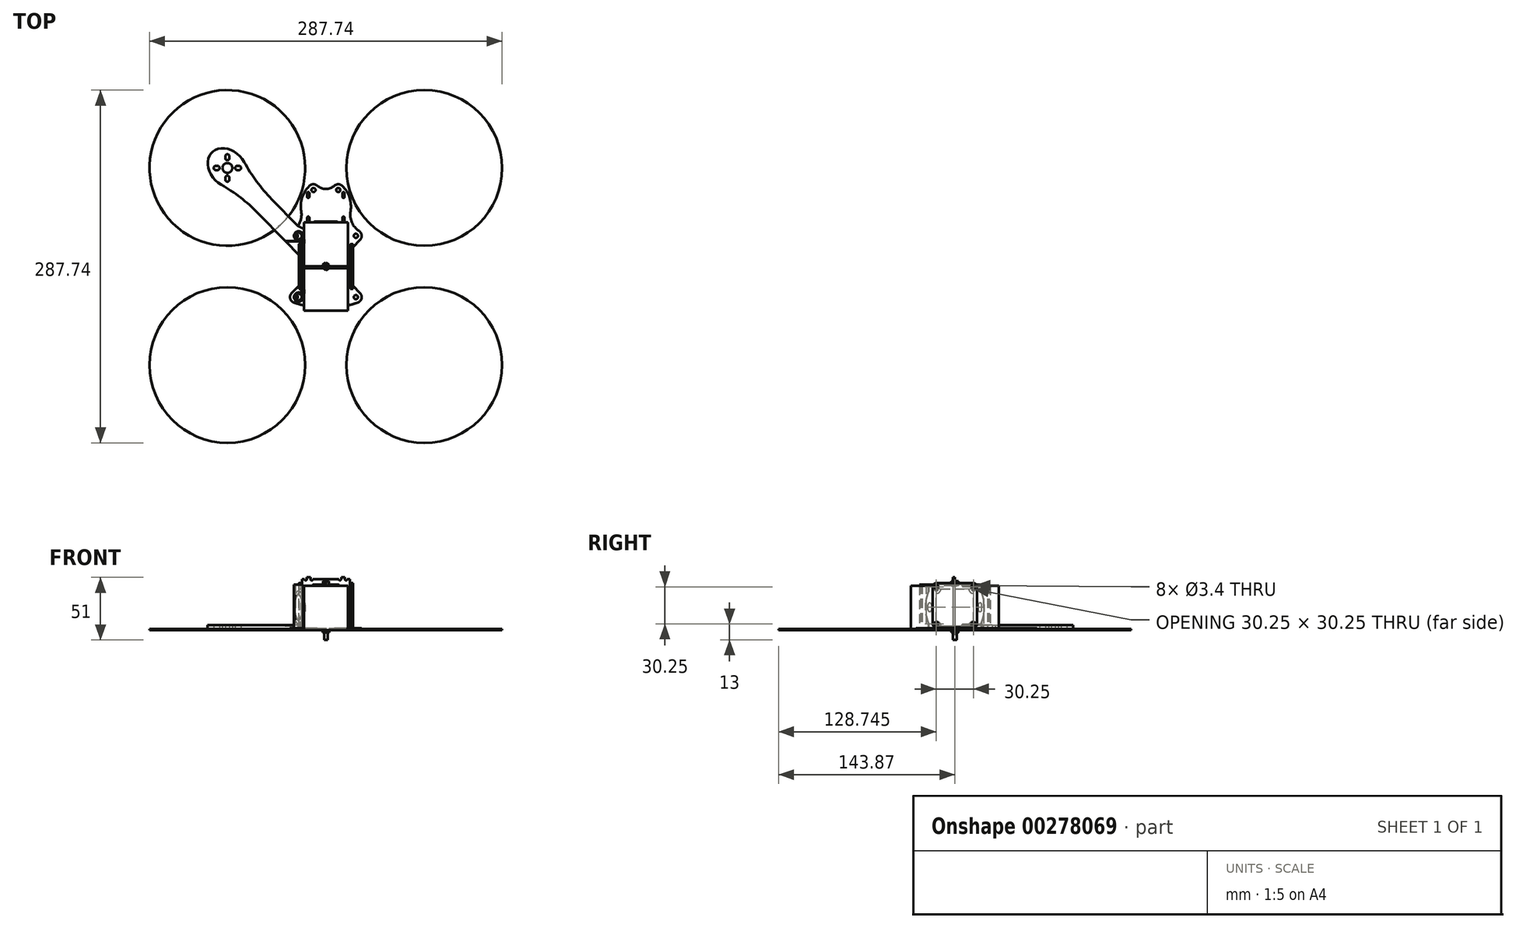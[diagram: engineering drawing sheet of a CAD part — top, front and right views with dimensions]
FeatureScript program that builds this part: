
annotation { "Feature Type Name" : "Feature", "Feature Type Description" : "" }
export const myFeature = defineFeature(function(context is Context, id is Id, definition is map)
    precondition{}
    {
        {
            var Q0;
            Q0=qCreatedBy(makeId("Top.planeOp"),FACE);
            var sketch = newSketch(context, id + "F0", { "sketchPlane" : qUnion([Q0])});
            skLineSegment(sketch, "E0.bottom", {"start": v(-18, 36) * mm, "end": v(18, 36) * mm});
            skLineSegment(sketch, "E0.top", {"start": v(-18, -36) * mm, "end": v(18, -36) * mm});
            skLineSegment(sketch, "E0.left", {"start": v(-18, 36) * mm, "end": v(-18, -36) * mm});
            skLineSegment(sketch, "E0.right", {"start": v(18, 36) * mm, "end": v(18, -36) * mm});
            skPoint(sketch, "E0.middle", {"position": v(0, 0) * mm});
            skSolve(sketch);
        }
        {
            var Q0;
            Q0 = qSketchRegion(id + "F0", true);
            extrude(context, id + "F1", {"entities" : qUnion([Q0]), "depth" : 36 * mm});
        }
        {
            var Q0;
            Q0=qCreatedBy(makeId("Right.planeOp"),FACE);
            cPlane(context, id + "F2", {"entities" : qUnion([Q0]), "cplaneType" : CPlaneType.OFFSET, "offset" : 20 * mm, "oppositeDirection" : true, "width" : 152.4 * mm, "height" : 152.4 * mm});
        }
        {
            var Q0;
            Q0=qCreatedBy(id+"F2.planeOp",FACE);
            var sketch = newSketch(context, id + "F3", { "sketchPlane" : qUnion([Q0])});
            skLineSegment(sketch, "E1.bottom", {"start": v(15.12, 38.25) * mm, "end": v(-15.12, 38.25) * mm});
            skLineSegment(sketch, "E1.top", {"start": v(15.13, 2) * mm, "end": v(-15.13, 2) * mm});
            skLineSegment(sketch, "E1.left", {"start": v(18.13, 35.25) * mm, "end": v(18.13, 5) * mm});
            skLineSegment(sketch, "E1.right", {"start": v(-18.12, 35.25) * mm, "end": v(-18.13, 5) * mm});
            skPoint(sketch, "E2.visualSharp", {"position": v(18.12, 38.25) * mm});
            skArc(sketch, "E2.filletArc", {"start": v(18.12, 35.25) * mm, "mid": v(17.25, 37.37) * mm, "end": v(15.12, 38.25) * mm});
            skPoint(sketch, "E3.visualSharp", {"position": v(-18.12, 38.25) * mm});
            skArc(sketch, "E3.filletArc", {"start": v(-15.12, 38.25) * mm, "mid": v(-17.25, 37.37) * mm, "end": v(-18.12, 35.25) * mm});
            skPoint(sketch, "E4.visualSharp", {"position": v(-18.13, 2) * mm});
            skArc(sketch, "E4.filletArc", {"start": v(-18.13, 5) * mm, "mid": v(-17.25, 2.88) * mm, "end": v(-15.13, 2) * mm});
            skPoint(sketch, "E5.visualSharp", {"position": v(18.13, 2) * mm});
            skArc(sketch, "E5.filletArc", {"start": v(15.13, 2) * mm, "mid": v(17.25, 2.88) * mm, "end": v(18.13, 5) * mm});
            skCircle(sketch, "E6", {"center": v(15.12, 35.25) * mm, "radius": 1.7 * mm});
            skCircle(sketch, "E7", {"center": v(15.13, 5) * mm, "radius": 1.7 * mm});
            skCircle(sketch, "E8", {"center": v(-15.12, 35.25) * mm, "radius": 1.7 * mm});
            skCircle(sketch, "E9", {"center": v(-15.13, 5) * mm, "radius": 1.7 * mm});
            skSolve(sketch);
        }
        {
            var Q0;
            Q0 = qSketchRegion(id + "F3", true);
            extrude(context, id + "F4", {"entities" : qUnion([Q0]), "oppositeDirection" : true, "depth" : 2 * mm});
        }
        {
            var Q0;
            Q0=makeQuery(id+"F4.opExtrude","SWEPT_BODY",BODY,{"disambiguationData":[OSD([sQuery(id+"F3.wireOp",EDGE,"E1.bottom"),sQuery(id+"F3.wireOp",EDGE,"E1.top"),sQuery(id+"F3.wireOp",EDGE,"E1.left"),sQuery(id+"F3.wireOp",EDGE,"E1.right"),sQuery(id+"F3.wireOp",EDGE,"E2.filletArc"),sQuery(id+"F3.wireOp",EDGE,"E3.filletArc"),sQuery(id+"F3.wireOp",EDGE,"E4.filletArc"),sQuery(id+"F3.wireOp",EDGE,"E5.filletArc"),sQuery(id+"F3.wireOp",EDGE,"E6"),sQuery(id+"F3.wireOp",EDGE,"E7"),sQuery(id+"F3.wireOp",EDGE,"E8"),sQuery(id+"F3.wireOp",EDGE,"E9")])]});
            var Q1;
            Q1=qCreatedBy(makeId("Right.planeOp"),FACE);
            mirror(context, id + "F5", {"entities" : qUnion([Q0]), "mirrorPlane" : qUnion([Q1])});
        }
        {
            var Q0;
            Q0=qCreatedBy(makeId("Top.planeOp"),FACE);
            var sketch = newSketch(context, id + "F6", { "sketchPlane" : qUnion([Q0])});
            skArc(sketch, "E10", {"start": v(-18.5, 25) * mm, "mid": v(-25.6, 26.68) * mm, "end": v(-20, 22) * mm});
            skArc(sketch, "E11", {"start": v(-20, -22) * mm, "mid": v(-25.6, -26.68) * mm, "end": v(-18.5, -25) * mm});
            skLineSegment(sketch, "E12", {"start": v(-18.5, 25) * mm, "end": v(-18.5, -25) * mm});
            skLineSegment(sketch, "E13", {"start": v(-20, 22) * mm, "end": v(-20, -22) * mm});
            skLineSegment(sketch, "E14.0", {"start": v(-22.25, 28.06) * mm, "end": v(-19.6, 26.53) * mm});
            skLineSegment(sketch, "E14.1", {"start": v(-19.6, 26.53) * mm, "end": v(-19.6, 23.47) * mm});
            skLineSegment(sketch, "E14.2", {"start": v(-19.6, 23.47) * mm, "end": v(-22.25, 21.94) * mm});
            skLineSegment(sketch, "E14.3", {"start": v(-22.25, 21.94) * mm, "end": v(-24.9, 23.47) * mm});
            skLineSegment(sketch, "E14.4", {"start": v(-24.9, 23.47) * mm, "end": v(-24.9, 26.53) * mm});
            skLineSegment(sketch, "E14.5", {"start": v(-24.9, 26.53) * mm, "end": v(-22.25, 28.06) * mm});
            skLineSegment(sketch, "E15.0", {"start": v(-22.25, -21.94) * mm, "end": v(-19.6, -23.47) * mm});
            skLineSegment(sketch, "E15.1", {"start": v(-19.6, -23.47) * mm, "end": v(-19.6, -26.53) * mm});
            skLineSegment(sketch, "E15.2", {"start": v(-19.6, -26.53) * mm, "end": v(-22.25, -28.06) * mm});
            skLineSegment(sketch, "E15.3", {"start": v(-22.25, -28.06) * mm, "end": v(-24.9, -26.53) * mm});
            skLineSegment(sketch, "E15.4", {"start": v(-24.9, -26.53) * mm, "end": v(-24.9, -23.47) * mm});
            skLineSegment(sketch, "E15.5", {"start": v(-24.9, -23.47) * mm, "end": v(-22.25, -21.94) * mm});
            skSolve(sketch);
        }
        {
            var Q0;
            Q0 = qSketchRegion(id + "F6", true);
            extrude(context, id + "F7", {"entities" : qUnion([Q0]), "depth" : 37 * mm});
        }
        {
            var Q0;
            Q0=makeQuery(id+"F7.opExtrude","SWEPT_FACE",FACE,{"disambiguationData":[OSD([sQuery(id+"F6.wireOp",EDGE,"E13")])]});
            var sketch = newSketch(context, id + "F8", { "sketchPlane" : qUnion([Q0])});
            skCircle(sketch, "E16", {"center": v(-15.13, 33.62) * mm, "radius": 1.73 * mm});
            skCircle(sketch, "E17", {"center": v(-15.13, 3.38) * mm, "radius": 1.73 * mm});
            skCircle(sketch, "E18", {"center": v(15.13, 33.62) * mm, "radius": 1.73 * mm});
            skCircle(sketch, "E19", {"center": v(15.12, 3.38) * mm, "radius": 1.73 * mm});
            skSolve(sketch);
        }
        {
            var Q0;
            Q0 = qSketchRegion(id + "F8", true);
            extrude(context, id + "F9", {"entities" : qUnion([Q0]), "operationType" : NewBodyOperationType.REMOVE, "oppositeDirection" : true, "depth" : 2 * mm});
        }
        {
            var Q0;
            Q0=makeQuery(id+"F7.opExtrude","SWEPT_BODY",BODY,{"disambiguationData":[OSD([sQuery(id+"F6.wireOp",EDGE,"E10"),sQuery(id+"F6.wireOp",EDGE,"E11"),sQuery(id+"F6.wireOp",EDGE,"E12"),sQuery(id+"F6.wireOp",EDGE,"E13"),sQuery(id+"F6.wireOp",EDGE,"E14.0"),sQuery(id+"F6.wireOp",EDGE,"E14.1"),sQuery(id+"F6.wireOp",EDGE,"E14.2"),sQuery(id+"F6.wireOp",EDGE,"E14.3"),sQuery(id+"F6.wireOp",EDGE,"E14.4"),sQuery(id+"F6.wireOp",EDGE,"E14.5"),sQuery(id+"F6.wireOp",EDGE,"E15.0"),sQuery(id+"F6.wireOp",EDGE,"E15.1"),sQuery(id+"F6.wireOp",EDGE,"E15.2"),sQuery(id+"F6.wireOp",EDGE,"E15.3"),sQuery(id+"F6.wireOp",EDGE,"E15.4"),sQuery(id+"F6.wireOp",EDGE,"E15.5")])]});
            transform(context, id + "F10", {"entities" : qUnion([Q0]), "transformType" : TransformType.TRANSLATION_3D, "dx" : 0 * mm, "dy" : 0 * mm, "dz" : 0 * mm, "makeCopy" : true});
        }
        {
            var Q0;
            Q0=makeQuery(id+"F7.opExtrude","SWEPT_FACE",FACE,{"disambiguationData":[OSD([sQuery(id+"F6.wireOp",EDGE,"E13")])]});
            var sketch = newSketch(context, id + "F11", { "sketchPlane" : qUnion([Q0])});
            skLineSegment(sketch, "E20", {"start": v(-15.13, 29.9) * mm, "end": v(-15.12, 7.1) * mm});
            skLineSegment(sketch, "E21", {"start": v(-11.4, 3.38) * mm, "end": v(11.4, 3.38) * mm});
            skLineSegment(sketch, "E22", {"start": v(15.12, 29.9) * mm, "end": v(15.13, 7.1) * mm});
            skLineSegment(sketch, "E23", {"start": v(-11.4, 33.62) * mm, "end": v(11.4, 33.62) * mm});
            skArc(sketch, "E24", {"start": v(15.13, 7.1) * mm, "mid": v(12.5, 6) * mm, "end": v(11.4, 3.38) * mm});
            skArc(sketch, "E25", {"start": v(11.4, 33.63) * mm, "mid": v(12.5, 31) * mm, "end": v(15.12, 29.9) * mm});
            skArc(sketch, "E26", {"start": v(-11.4, 33.62) * mm, "mid": v(-12.5, 31) * mm, "end": v(-15.13, 29.9) * mm});
            skArc(sketch, "E27", {"start": v(-15.13, 7.1) * mm, "mid": v(-12.5, 6) * mm, "end": v(-11.4, 3.38) * mm});
            skSolve(sketch);
        }
        {
            var Q0;
            Q0 = qSketchRegion(id + "F11", true);
            extrude(context, id + "F12", {"entities" : qUnion([Q0]), "operationType" : NewBodyOperationType.REMOVE, "oppositeDirection" : true, "depth" : 2 * mm});
        }
        {
            var Q0;
            Q0=qCreatedBy(makeId("Top.planeOp"),FACE);
            var sketch = newSketch(context, id + "F13", { "sketchPlane" : qUnion([Q0])});
            skCircle(sketch, "E28.cCircle", {"center": v(0, 0) * mm, "radius": 2.5 * mm, "construction": true});
            skLineSegment(sketch, "E28.0", {"start": v(-2.5, 1.44) * mm, "end": v(0, 2.89) * mm});
            skLineSegment(sketch, "E28.1", {"start": v(0, 2.89) * mm, "end": v(2.5, 1.44) * mm});
            skLineSegment(sketch, "E28.2", {"start": v(2.5, 1.44) * mm, "end": v(2.5, -1.44) * mm});
            skLineSegment(sketch, "E28.3", {"start": v(2.5, -1.44) * mm, "end": v(0, -2.89) * mm});
            skLineSegment(sketch, "E28.4", {"start": v(0, -2.89) * mm, "end": v(-2.5, -1.44) * mm});
            skLineSegment(sketch, "E28.5", {"start": v(-2.5, -1.44) * mm, "end": v(-2.5, 1.44) * mm});
            skPoint(sketch, "E28.0.midPoint", {"position": v(-1.25, 2.17) * mm});
            skCircle(sketch, "E29", {"center": v(0, 0) * mm, "radius": 1.65 * mm});
            skSolve(sketch);
        }
        {
            var Q0;
            Q0 = qSketchRegion(id + "F13", true);
            extrude(context, id + "F14", {"entities" : qUnion([Q0]), "depth" : 40 * mm});
        }
        {
            var Q0;
            Q0=qCreatedBy(makeId("Top.planeOp"),FACE);
            var sketch = newSketch(context, id + "F15", { "sketchPlane" : qUnion([Q0])});
            skCircle(sketch, "E30", {"center": v(0, 0) * mm, "radius": 2.75 * mm});
            skCircle(sketch, "E31.cCircle", {"center": v(0, 0) * mm, "radius": 1.15 * mm, "construction": true});
            skLineSegment(sketch, "E31.0", {"start": v(-0.58, 1) * mm, "end": v(0.58, 1) * mm});
            skLineSegment(sketch, "E31.1", {"start": v(0.58, 1) * mm, "end": v(1.15, 0) * mm});
            skLineSegment(sketch, "E31.2", {"start": v(1.15, 0) * mm, "end": v(0.58, -1) * mm});
            skLineSegment(sketch, "E31.3", {"start": v(0.58, -1) * mm, "end": v(-0.58, -1) * mm});
            skLineSegment(sketch, "E31.4", {"start": v(-0.58, -1) * mm, "end": v(-1.15, 0) * mm});
            skLineSegment(sketch, "E31.5", {"start": v(-1.15, 0) * mm, "end": v(-0.58, 1) * mm});
            skCircle(sketch, "E32", {"center": v(0, 0) * mm, "radius": 1.5 * mm});
            skSolve(sketch);
        }
        {
            var Q0;
            Q0=makeQuery(id+"F15.imprint","IMPRINT",FACE,{"disambiguationData":[TD([[makeQuery(id+"F15.imprint","IMPRINT",EDGE,{"derivedFrom":sQuery(id+"F15.wireOp",EDGE,"E31.0")}),1.0]])]});
            var Q1;
            Q1=makeQuery(id+"F15.imprint","IMPRINT",FACE,{"disambiguationData":[TD([[makeQuery(id+"F15.imprint","IMPRINT",EDGE,{"derivedFrom":sQuery(id+"F15.wireOp",EDGE,"E31.0")}),-1.0]])]});
            extrude(context, id + "F16", {"entities" : qUnion([Q0, Q1]), "oppositeDirection" : true, "depth" : 8 * mm});
        }
        {
            var Q0;
            Q0=makeQuery(id+"F15.imprint","IMPRINT",FACE,{"disambiguationData":[TD([[makeQuery(id+"F15.imprint","IMPRINT",EDGE,{"derivedFrom":sQuery(id+"F15.wireOp",EDGE,"E30")}),1.0]])]});
            var Q1;
            Q1=makeQuery(id+"F15.imprint","IMPRINT",FACE,{"disambiguationData":[TD([[makeQuery(id+"F15.imprint","IMPRINT",EDGE,{"derivedFrom":sQuery(id+"F15.wireOp",EDGE,"E31.0")}),1.0]])]});
            var Q2;
            Q2=makeQuery(id+"F15.imprint","IMPRINT",FACE,{"disambiguationData":[TD([[makeQuery(id+"F15.imprint","IMPRINT",EDGE,{"derivedFrom":sQuery(id+"F15.wireOp",EDGE,"E31.0")}),-1.0]])]});
            extrude(context, id + "F17", {"entities" : qUnion([Q0, Q1, Q2]), "operationType" : NewBodyOperationType.ADD, "oppositeDirection" : true, "depth" : 2 * mm});
        }
        {
            var Q0;
            Q0=makeQuery(id+"F15.imprint","IMPRINT",FACE,{"disambiguationData":[TD([[makeQuery(id+"F15.imprint","IMPRINT",EDGE,{"derivedFrom":sQuery(id+"F15.wireOp",EDGE,"E31.0")}),-1.0]])]});
            extrude(context, id + "F18", {"entities" : qUnion([Q0]), "operationType" : NewBodyOperationType.REMOVE, "oppositeDirection" : true, "depth" : 1.5 * mm});
        }
        {
            var Q0;
            Q0=qCreatedBy(makeId("Top.planeOp"),FACE);
            var sketch = newSketch(context, id + "F19", { "sketchPlane" : qUnion([Q0])});
            skCircle(sketch, "E33.cCircle", {"center": v(0, 0) * mm, "radius": 3.18 * mm, "construction": true});
            skLineSegment(sketch, "E33.0", {"start": v(-1.59, 2.75) * mm, "end": v(1.59, 2.75) * mm});
            skLineSegment(sketch, "E33.1", {"start": v(1.59, 2.75) * mm, "end": v(3.18, 0) * mm});
            skLineSegment(sketch, "E33.2", {"start": v(3.18, 0) * mm, "end": v(1.59, -2.75) * mm});
            skLineSegment(sketch, "E33.3", {"start": v(1.59, -2.75) * mm, "end": v(-1.59, -2.75) * mm});
            skLineSegment(sketch, "E33.4", {"start": v(-1.59, -2.75) * mm, "end": v(-3.18, 0) * mm});
            skLineSegment(sketch, "E33.5", {"start": v(-3.18, 0) * mm, "end": v(-1.59, 2.75) * mm});
            skCircle(sketch, "E34", {"center": v(0, 0) * mm, "radius": 1.5 * mm});
            skSolve(sketch);
        }
        {
            var Q0;
            Q0 = qSketchRegion(id + "F19", true);
            extrude(context, id + "F20", {"entities" : qUnion([Q0]), "depth" : 1.8 * mm});
        }
        {
            var Q0;
            Q0=makeQuery(id+"F10.opPattern","COPY",FACE,{"derivedFrom":makeQuery(id+"F7.opExtrude","SWEPT_FACE",FACE,{"disambiguationData":[OSD([sQuery(id+"F6.wireOp",EDGE,"E13")])]}),"instanceName":"1"});
            var sketch = newSketch(context, id + "F21", { "sketchPlane" : qUnion([Q0])});
            skLineSegment(sketch, "E35", {"start": v(-22, 20.5) * mm, "end": v(-22, 16.5) * mm});
            skLineSegment(sketch, "E36", {"start": v(-19, 16.5) * mm, "end": v(-19, 20.5) * mm});
            skLineSegment(sketch, "E37", {"start": v(22, 20.5) * mm, "end": v(22, 16.5) * mm});
            skLineSegment(sketch, "E38", {"start": v(19, 16.5) * mm, "end": v(19, 20.5) * mm});
            skArc(sketch, "E39", {"start": v(-22, 20.5) * mm, "mid": v(-20.5, 22) * mm, "end": v(-19, 20.5) * mm});
            skArc(sketch, "E40", {"start": v(19, 20.5) * mm, "mid": v(20.5, 22) * mm, "end": v(22, 20.5) * mm});
            skArc(sketch, "E41", {"start": v(-19, 16.5) * mm, "mid": v(-20.5, 15) * mm, "end": v(-22, 16.5) * mm});
            skArc(sketch, "E42", {"start": v(19, 16.5) * mm, "mid": v(20.5, 15) * mm, "end": v(22, 16.5) * mm});
            skSolve(sketch);
        }
        {
            var Q0;
            Q0=qCreatedBy(makeId("Top.planeOp"),FACE);
            var sketch = newSketch(context, id + "F22", { "sketchPlane" : qUnion([Q0])});
            skCircle(sketch, "E43", {"center": v(-24.5, 25) * mm, "radius": 1.7 * mm});
            skCircle(sketch, "E44", {"center": v(24.5, 25) * mm, "radius": 1.7 * mm});
            skCircle(sketch, "E45", {"center": v(24.5, -25) * mm, "radius": 1.7 * mm});
            skCircle(sketch, "E46", {"center": v(-24.5, -25) * mm, "radius": 1.7 * mm});
            skLineSegment(sketch, "E47", {"start": v(-18, 11.62) * mm, "end": v(-18, -11.62) * mm});
            skLineSegment(sketch, "E48", {"start": v(18, 11.62) * mm, "end": v(18, -11.62) * mm});
            skLineSegment(sketch, "E49", {"start": v(18, 11.62) * mm, "end": v(27.87, 21.7) * mm});
            skLineSegment(sketch, "E50", {"start": v(18, -11.62) * mm, "end": v(27.87, -21.7) * mm});
            skLineSegment(sketch, "E51", {"start": v(-18, -11.62) * mm, "end": v(-27.87, -21.7) * mm});
            skLineSegment(sketch, "E52", {"start": v(-18, 11.62) * mm, "end": v(-27.87, 21.7) * mm});
            skArc(sketch, "E53", {"start": v(-27.87, 21.7) * mm, "mid": v(-29.2, 25.5) * mm, "end": v(-27.1, 28.94) * mm});
            skArc(sketch, "E54", {"start": v(27.87, 21.7) * mm, "mid": v(29.2, 25.5) * mm, "end": v(27.1, 28.94) * mm});
            skArc(sketch, "E55", {"start": v(27.87, -21.7) * mm, "mid": v(29.1, -26.09) * mm, "end": v(26.04, -29.47) * mm});
            skArc(sketch, "E56", {"start": v(-27.87, -21.7) * mm, "mid": v(-29.1, -26.09) * mm, "end": v(-26.04, -29.47) * mm});
            skArc(sketch, "E57", {"start": v(-26.04, -29.47) * mm, "mid": v(0, -33.82) * mm, "end": v(26.04, -29.47) * mm});
            skLineSegment(sketch, "E58", {"start": v(-10, -25) * mm, "end": v(10, -25) * mm});
            skLineSegment(sketch, "E59", {"start": v(10, -27.5) * mm, "end": v(-10, -27.5) * mm});
            skArc(sketch, "E60", {"start": v(-10, -27.5) * mm, "mid": v(-11.25, -26.25) * mm, "end": v(-10, -25) * mm});
            skArc(sketch, "E61", {"start": v(10, -27.5) * mm, "mid": v(11.25, -26.25) * mm, "end": v(10, -25) * mm});
            skLineSegment(sketch, "E62", {"start": v(-15.3, 36.8) * mm, "end": v(-15.3, 39.8) * mm});
            skLineSegment(sketch, "E63", {"start": v(-13.5, 39.8) * mm, "end": v(-13.5, 36.8) * mm});
            skArc(sketch, "E64", {"start": v(-15.3, 39.8) * mm, "mid": v(-14.4, 40.7) * mm, "end": v(-13.5, 39.8) * mm});
            skArc(sketch, "E65", {"start": v(-13.5, 36.8) * mm, "mid": v(-14.4, 35.9) * mm, "end": v(-15.3, 36.8) * mm});
            skLineSegment(sketch, "E66", {"start": v(13.5, 39.8) * mm, "end": v(13.5, 36.8) * mm});
            skLineSegment(sketch, "E67", {"start": v(15.3, 39.8) * mm, "end": v(15.3, 36.8) * mm});
            skArc(sketch, "E68", {"start": v(15.3, 39.8) * mm, "mid": v(14.4, 40.7) * mm, "end": v(13.5, 39.8) * mm});
            skArc(sketch, "E69", {"start": v(15.3, 36.8) * mm, "mid": v(14.4, 35.9) * mm, "end": v(13.5, 36.8) * mm});
            skLineSegment(sketch, "E70", {"start": v(-15.3, 59.8) * mm, "end": v(-15.3, 56.8) * mm});
            skLineSegment(sketch, "E71", {"start": v(-13.5, 59.8) * mm, "end": v(-13.5, 56.8) * mm});
            skLineSegment(sketch, "E72", {"start": v(13.5, 59.8) * mm, "end": v(13.5, 56.8) * mm});
            skLineSegment(sketch, "E73", {"start": v(15.3, 59.8) * mm, "end": v(15.3, 56.8) * mm});
            skArc(sketch, "E74", {"start": v(-15.3, 59.8) * mm, "mid": v(-14.4, 60.7) * mm, "end": v(-13.5, 59.8) * mm});
            skArc(sketch, "E75", {"start": v(-13.5, 56.8) * mm, "mid": v(-14.4, 55.9) * mm, "end": v(-15.3, 56.8) * mm});
            skArc(sketch, "E76", {"start": v(13.5, 59.8) * mm, "mid": v(14.4, 60.7) * mm, "end": v(15.3, 59.8) * mm});
            skArc(sketch, "E77", {"start": v(15.3, 56.8) * mm, "mid": v(14.4, 55.9) * mm, "end": v(13.5, 56.8) * mm});
            skLineSegment(sketch, "E78", {"start": v(-15.5, 30) * mm, "end": v(-12.5, 30) * mm});
            skLineSegment(sketch, "E79", {"start": v(-15.5, 31.8) * mm, "end": v(-12.5, 31.8) * mm});
            skLineSegment(sketch, "E80", {"start": v(12.5, 31.8) * mm, "end": v(15.5, 31.8) * mm});
            skLineSegment(sketch, "E81", {"start": v(15.5, 30) * mm, "end": v(12.5, 30) * mm});
            skArc(sketch, "E82", {"start": v(-12.5, 31.8) * mm, "mid": v(-11.6, 30.9) * mm, "end": v(-12.5, 30) * mm});
            skArc(sketch, "E83", {"start": v(-15.5, 31.8) * mm, "mid": v(-16.4, 30.9) * mm, "end": v(-15.5, 30) * mm});
            skArc(sketch, "E84", {"start": v(12.5, 31.8) * mm, "mid": v(11.6, 30.9) * mm, "end": v(12.5, 30) * mm});
            skArc(sketch, "E85", {"start": v(15.5, 31.8) * mm, "mid": v(16.4, 30.9) * mm, "end": v(15.5, 30) * mm});
            skCircle(sketch, "E86", {"center": v(-10.13, 62.4) * mm, "radius": 1.7 * mm});
            skCircle(sketch, "E87", {"center": v(10.13, 62.4) * mm, "radius": 1.7 * mm});
            skArc(sketch, "E88", {"start": v(-13.4, 65.78) * mm, "mid": v(-10.23, 67.1) * mm, "end": v(-7.01, 65.92) * mm});
            skArc(sketch, "E89", {"start": v(13.4, 65.78) * mm, "mid": v(10.23, 67.1) * mm, "end": v(7.01, 65.92) * mm});
            skArc(sketch, "E90", {"start": v(-7.01, 65.92) * mm, "mid": v(0, 63.26) * mm, "end": v(7.01, 65.92) * mm});
            skArc(sketch, "E91", {"start": v(-27.1, 28.94) * mm, "mid": v(-21.2, 36) * mm, "end": v(-20.12, 45.13) * mm});
            skArc(sketch, "E92", {"start": v(27.1, 28.94) * mm, "mid": v(21.2, 36) * mm, "end": v(20.12, 45.13) * mm});
            skLineSegment(sketch, "E93", {"start": v(-9, 34.02) * mm, "end": v(9, 34.02) * mm});
            skLineSegment(sketch, "E94", {"start": v(-9, 36.52) * mm, "end": v(9, 36.52) * mm});
            skArc(sketch, "E95", {"start": v(-9, 36.52) * mm, "mid": v(-10.25, 35.27) * mm, "end": v(-9, 34.02) * mm});
            skArc(sketch, "E96", {"start": v(9, 36.52) * mm, "mid": v(10.25, 35.27) * mm, "end": v(9, 34.02) * mm});
            skLineSegment(sketch, "E97", {"start": v(-9, 27.02) * mm, "end": v(9, 27.02) * mm});
            skLineSegment(sketch, "E98", {"start": v(-9, 24.52) * mm, "end": v(9, 24.52) * mm});
            skArc(sketch, "E99", {"start": v(-9, 27.02) * mm, "mid": v(-10.25, 25.77) * mm, "end": v(-9, 24.52) * mm});
            skArc(sketch, "E100", {"start": v(9, 27.02) * mm, "mid": v(10.25, 25.77) * mm, "end": v(9, 24.52) * mm});
            skCircle(sketch, "E101", {"center": v(-12.5, 17.5) * mm, "radius": 1.7 * mm});
            skCircle(sketch, "E102", {"center": v(-7.5, 5) * mm, "radius": 1.7 * mm});
            skCircle(sketch, "E103", {"center": v(12.5, 17.5) * mm, "radius": 1.7 * mm});
            skCircle(sketch, "E104", {"center": v(7.5, 5) * mm, "radius": 1.7 * mm});
            skCircle(sketch, "E105", {"center": v(-7.5, -5) * mm, "radius": 1.7 * mm});
            skCircle(sketch, "E106", {"center": v(7.5, -5) * mm, "radius": 1.7 * mm});
            skCircle(sketch, "E107", {"center": v(-12.5, -17.5) * mm, "radius": 1.7 * mm});
            skCircle(sketch, "E108", {"center": v(12.5, -17.5) * mm, "radius": 1.7 * mm});
            skArc(sketch, "E109", {"start": v(20.12, 45.13) * mm, "mid": v(19.32, 56.3) * mm, "end": v(13.4, 65.78) * mm});
            skArc(sketch, "E110", {"start": v(-13.4, 65.78) * mm, "mid": v(-19.32, 56.3) * mm, "end": v(-20.12, 45.13) * mm});
            skSolve(sketch);
        }
        {
            var Q0;
            Q0 = qSketchRegion(id + "F22", true);
            extrude(context, id + "F23", {"entities" : qUnion([Q0]), "depth" : 1.5 * mm});
        }
        {
            var Q0;
            Q0=qCreatedBy(makeId("Top.planeOp"),FACE);
            var sketch = newSketch(context, id + "F24", { "sketchPlane" : qUnion([Q0])});
            skLineSegment(sketch, "E111", {"start": v(0, 0) * mm, "end": v(-12.73, 0) * mm});
            skLineSegment(sketch, "E112", {"start": v(-12.73, 0) * mm, "end": v(-55.49, 43.63) * mm});
            skLineSegment(sketch, "E113", {"start": v(0, 0) * mm, "end": v(0, 12.73) * mm});
            skArc(sketch, "E114", {"start": v(0, 12.73) * mm, "mid": v(-10.03, 24.45) * mm, "end": v(-22.8, 33.13) * mm});
            skCircle(sketch, "E115", {"center": v(-80.37, 80.37) * mm, "radius": 4 * mm});
            skLineSegment(sketch, "E116", {"start": v(-82.07, 72.37) * mm, "end": v(-82.07, 70.87) * mm});
            skLineSegment(sketch, "E117", {"start": v(-78.67, 72.37) * mm, "end": v(-78.67, 70.87) * mm});
            skArc(sketch, "E118", {"start": v(-82.07, 70.87) * mm, "mid": v(-80.37, 69.17) * mm, "end": v(-78.67, 70.87) * mm});
            skArc(sketch, "E119", {"start": v(-78.67, 72.37) * mm, "mid": v(-80.37, 74.07) * mm, "end": v(-82.07, 72.37) * mm});
            skLineSegment(sketch, "E120", {"start": v(-72.37, 78.67) * mm, "end": v(-70.87, 78.67) * mm});
            skLineSegment(sketch, "E121", {"start": v(-70.87, 82.07) * mm, "end": v(-72.37, 82.07) * mm});
            skLineSegment(sketch, "E122", {"start": v(-78.67, 88.37) * mm, "end": v(-78.67, 89.87) * mm});
            skLineSegment(sketch, "E123", {"start": v(-82.07, 89.87) * mm, "end": v(-82.07, 88.37) * mm});
            skLineSegment(sketch, "E124", {"start": v(-88.37, 82.07) * mm, "end": v(-89.87, 82.07) * mm});
            skLineSegment(sketch, "E125", {"start": v(-88.37, 78.67) * mm, "end": v(-89.87, 78.67) * mm});
            skArc(sketch, "E126", {"start": v(-82.07, 89.87) * mm, "mid": v(-80.37, 91.57) * mm, "end": v(-78.67, 89.87) * mm});
            skArc(sketch, "E127", {"start": v(-78.67, 88.37) * mm, "mid": v(-80.37, 86.67) * mm, "end": v(-82.07, 88.37) * mm});
            skArc(sketch, "E128", {"start": v(-72.37, 82.07) * mm, "mid": v(-74.07, 80.37) * mm, "end": v(-72.37, 78.67) * mm});
            skArc(sketch, "E129", {"start": v(-70.87, 82.07) * mm, "mid": v(-69.17, 80.37) * mm, "end": v(-70.87, 78.67) * mm});
            skArc(sketch, "E130", {"start": v(-89.87, 82.07) * mm, "mid": v(-91.57, 80.37) * mm, "end": v(-89.87, 78.67) * mm});
            skArc(sketch, "E131", {"start": v(-88.37, 82.07) * mm, "mid": v(-86.67, 80.37) * mm, "end": v(-88.37, 78.67) * mm});
            skLineSegment(sketch, "E132", {"start": v(-90.37, 70.57) * mm, "end": v(-70.37, 90.17) * mm});
            skLineSegment(sketch, "E133", {"start": v(-92.97, 93.23) * mm, "end": v(-67.78, 67.52) * mm});
            skEllipse(sketch, "E134", {"center": v(-80.37, 80.37) * mm, "majorRadius": 18 * mm, "minorRadius": 14 * mm, "majorAxis": v(-0.7, 0.71)});
            skArc(sketch, "E135", {"start": v(-55.49, 43.63) * mm, "mid": v(-69.67, 56.24) * mm, "end": v(-85.45, 66.77) * mm});
            skLineSegment(sketch, "E136", {"start": v(-22.8, 33.13) * mm, "end": v(-44.06, 54.83) * mm});
            skArc(sketch, "E137", {"start": v(-44.06, 54.83) * mm, "mid": v(-56.42, 69.29) * mm, "end": v(-66.72, 85.28) * mm});
            skLineSegment(sketch, "E138", {"start": v(-55.49, 43.63) * mm, "end": v(-44.06, 54.83) * mm});
            skCircle(sketch, "E139", {"center": v(-24.5, 25) * mm, "radius": 1.7 * mm});
            skCircle(sketch, "E140", {"center": v(-12.5, 17.5) * mm, "radius": 1.7 * mm});
            skCircle(sketch, "E141", {"center": v(-7.5, 5) * mm, "radius": 1.7 * mm});
            skSolve(sketch);
        }
        {
            var Q0;
            Q0=qCreatedBy(makeId("Top.planeOp"),FACE);
            var sketch = newSketch(context, id + "F25", { "sketchPlane" : qUnion([Q0])});
            skCircle(sketch, "E142", {"center": v(-80.37, 80.37) * mm, "radius": 63.5 * mm});
            skCircle(sketch, "E143", {"center": v(80.37, 80.37) * mm, "radius": 63.5 * mm});
            skCircle(sketch, "E144", {"center": v(-80.37, -80.37) * mm, "radius": 63.5 * mm});
            skCircle(sketch, "E145", {"center": v(80.37, -80.37) * mm, "radius": 63.5 * mm});
            skSolve(sketch);
        }
        {
            var Q0;
            Q0 = qSketchRegion(id + "F25", true);
            extrude(context, id + "F26", {"entities" : qUnion([Q0]), "depth" : 1 * mm});
        }
        {
            var Q0;
            Q0 = qSketchRegion(id + "F24", true);
            extrude(context, id + "F27", {"entities" : qUnion([Q0]), "depth" : 4 * mm});
        }
        {
            var Q0;
            Q0=makeQuery(id+"F7.opExtrude","SWEPT_FACE",FACE,{"disambiguationData":[OSD([sQuery(id+"F6.wireOp",EDGE,"E13")])]});
            var sketch = newSketch(context, id + "F28", { "sketchPlane" : qUnion([Q0])});
            skLineSegment(sketch, "E146", {"start": v(-20.55, 33.5) * mm, "end": v(-20.55, 3.5) * mm});
            skLineSegment(sketch, "E147", {"start": v(20.55, 33.5) * mm, "end": v(20.55, 3.5) * mm});
            skArc(sketch, "E148", {"start": v(-20.55, 33.5) * mm, "mid": v(-23.92, 18.5) * mm, "end": v(-20.55, 3.5) * mm});
            skArc(sketch, "E149", {"start": v(20.55, 3.5) * mm, "mid": v(23.92, 18.5) * mm, "end": v(20.55, 33.5) * mm});
            skSolve(sketch);
        }
        {
            var Q0;
            Q0 = qSketchRegion(id + "F28", true);
            extrude(context, id + "F29", {"entities" : qUnion([Q0]), "operationType" : NewBodyOperationType.REMOVE, "depth" : 25.4 * mm});
        }
        {
            var Q0;
            Q0=makeQuery(id+"F10.opPattern","COPY",BODY,{"derivedFrom":makeQuery(id+"F7.opExtrude","SWEPT_BODY",BODY,{"disambiguationData":[OSD([sQuery(id+"F6.wireOp",EDGE,"E10"),sQuery(id+"F6.wireOp",EDGE,"E11"),sQuery(id+"F6.wireOp",EDGE,"E12"),sQuery(id+"F6.wireOp",EDGE,"E13"),sQuery(id+"F6.wireOp",EDGE,"E14.0"),sQuery(id+"F6.wireOp",EDGE,"E14.1"),sQuery(id+"F6.wireOp",EDGE,"E14.2"),sQuery(id+"F6.wireOp",EDGE,"E14.3"),sQuery(id+"F6.wireOp",EDGE,"E14.4"),sQuery(id+"F6.wireOp",EDGE,"E14.5"),sQuery(id+"F6.wireOp",EDGE,"E15.0"),sQuery(id+"F6.wireOp",EDGE,"E15.1"),sQuery(id+"F6.wireOp",EDGE,"E15.2"),sQuery(id+"F6.wireOp",EDGE,"E15.3"),sQuery(id+"F6.wireOp",EDGE,"E15.4"),sQuery(id+"F6.wireOp",EDGE,"E15.5")])]}),"instanceName":"1"});
            deleteBodies(context, id + "F30", {"entities" : qUnion([Q0])});
        }
        {
            var Q0;
            Q0 = qSketchRegion(id + "F21", true);
            extrude(context, id + "F31", {"entities" : qUnion([Q0]), "operationType" : NewBodyOperationType.REMOVE, "oppositeDirection" : true, "depth" : 3 * mm});
        }
        {
            var Q0;
            Q0=qCreatedBy(makeId("Front.planeOp"),FACE);
            var sketch = newSketch(context, id + "F32", { "sketchPlane" : qUnion([Q0])});
            skLineSegment(sketch, "E150.bottom", {"start": v(-19.5, 41.5) * mm, "end": v(-17.5, 41.5) * mm});
            skLineSegment(sketch, "E150.top", {"start": v(-19.5, 1.5) * mm, "end": v(-17.5, 1.5) * mm});
            skLineSegment(sketch, "E150.left", {"start": v(-19.5, 41.5) * mm, "end": v(-19.5, 1.5) * mm});
            skLineSegment(sketch, "E150.right", {"start": v(19.5, 41.5) * mm, "end": v(19.5, 1.5) * mm});
            skLineSegment(sketch, "E151.bottom", {"start": v(-15.5, 43) * mm, "end": v(-12.5, 43) * mm});
            skLineSegment(sketch, "E151.top", {"start": v(-15.5, 0) * mm, "end": v(-12.5, 0) * mm});
            skLineSegment(sketch, "E151.left", {"start": v(-15.5, 43) * mm, "end": v(-15.5, 41.5) * mm});
            skLineSegment(sketch, "E151.right", {"start": v(-12.5, 43) * mm, "end": v(-12.5, 41.5) * mm});
            skLineSegment(sketch, "E152.bottom", {"start": v(12.5, 43) * mm, "end": v(15.5, 43) * mm});
            skLineSegment(sketch, "E152.top", {"start": v(12.5, 0) * mm, "end": v(15.5, 0) * mm});
            skLineSegment(sketch, "E152.left", {"start": v(12.5, 43) * mm, "end": v(12.5, 41.5) * mm});
            skLineSegment(sketch, "E152.right", {"start": v(15.5, 43) * mm, "end": v(15.5, 41.5) * mm});
            skLineSegment(sketch, "E153.trimOffspring", {"start": v(12.5, 1.5) * mm, "end": v(12.5, 0) * mm});
            skLineSegment(sketch, "E154.trimOffspring", {"start": v(17.5, 41.5) * mm, "end": v(19.5, 41.5) * mm});
            skLineSegment(sketch, "E155.trimOffspring", {"start": v(15.5, 1.5) * mm, "end": v(15.5, 0) * mm});
            skLineSegment(sketch, "E156.trimOffspring", {"start": v(17.5, 1.5) * mm, "end": v(19.5, 1.5) * mm});
            skLineSegment(sketch, "E157.trimOffspring", {"start": v(-12.5, 1.5) * mm, "end": v(-12.5, 0) * mm});
            skLineSegment(sketch, "E158.trimOffspring", {"start": v(-15.5, 1.5) * mm, "end": v(-15.5, 0) * mm});
            skLineSegment(sketch, "E159.trimOffspring", {"start": v(-10.5, 41.5) * mm, "end": v(10.5, 41.5) * mm});
            skArc(sketch, "E160", {"start": v(-17.5, 41.5) * mm, "mid": v(-16.5, 40.5) * mm, "end": v(-15.5, 41.5) * mm});
            skArc(sketch, "E161", {"start": v(-12.5, 41.5) * mm, "mid": v(-11.5, 40.5) * mm, "end": v(-10.5, 41.5) * mm});
            skArc(sketch, "E162", {"start": v(10.5, 41.5) * mm, "mid": v(11.5, 40.5) * mm, "end": v(12.5, 41.5) * mm});
            skArc(sketch, "E163", {"start": v(15.5, 41.5) * mm, "mid": v(16.5, 40.5) * mm, "end": v(17.5, 41.5) * mm});
            skArc(sketch, "E164", {"start": v(17.5, 1.5) * mm, "mid": v(16.5, 2.5) * mm, "end": v(15.5, 1.5) * mm});
            skArc(sketch, "E165", {"start": v(12.5, 1.5) * mm, "mid": v(11.5, 2.5) * mm, "end": v(10.5, 1.5) * mm});
            skArc(sketch, "E166", {"start": v(-10.5, 1.5) * mm, "mid": v(-11.5, 2.5) * mm, "end": v(-12.5, 1.5) * mm});
            skArc(sketch, "E167", {"start": v(-15.5, 1.5) * mm, "mid": v(-16.5, 2.5) * mm, "end": v(-17.5, 1.5) * mm});
            skLineSegment(sketch, "E168.trimOffspring", {"start": v(11.5, 1.5) * mm, "end": v(12.5, 1.5) * mm});
            skLineSegment(sketch, "E169", {"start": v(-10.5, 1.5) * mm, "end": v(10.5, 1.5) * mm});
            skLineSegment(sketch, "E170", {"start": v(-10, 37) * mm, "end": v(10, 37) * mm});
            skLineSegment(sketch, "E171", {"start": v(10, 34.5) * mm, "end": v(-10, 34.5) * mm});
            skArc(sketch, "E172", {"start": v(-10, 37) * mm, "mid": v(-11.25, 35.75) * mm, "end": v(-10, 34.5) * mm});
            skArc(sketch, "E173", {"start": v(10, 37) * mm, "mid": v(11.25, 35.75) * mm, "end": v(10, 34.5) * mm});
            skLineSegment(sketch, "E174.bottom", {"start": v(-12.14, 29.5) * mm, "end": v(12.14, 29.5) * mm});
            skLineSegment(sketch, "E174.top", {"start": v(-12.14, 6.5) * mm, "end": v(12.14, 6.5) * mm});
            skLineSegment(sketch, "E174.left", {"start": v(-15.5, 27) * mm, "end": v(-15.5, 9) * mm});
            skLineSegment(sketch, "E174.right", {"start": v(15.5, 27) * mm, "end": v(15.5, 9) * mm});
            skLineSegment(sketch, "E175", {"start": v(-12.14, 29.5) * mm, "end": v(0, 20.5) * mm});
            skLineSegment(sketch, "E176", {"start": v(-15.5, 27) * mm, "end": v(-3.36, 18) * mm});
            skLineSegment(sketch, "E177", {"start": v(12.14, 29.5) * mm, "end": v(0, 20.5) * mm});
            skLineSegment(sketch, "E178", {"start": v(15.5, 27) * mm, "end": v(3.36, 18) * mm});
            skPoint(sketch, "E179.orphan", {"position": v(-15.5, 29.5) * mm});
            skPoint(sketch, "E180.orphan", {"position": v(15.5, 29.5) * mm});
            skPoint(sketch, "E181.orphan", {"position": v(15.5, 6.5) * mm});
            skPoint(sketch, "E182.orphan", {"position": v(-15.5, 6.5) * mm});
            skLineSegment(sketch, "E183.trimOffspring", {"start": v(0, 15.5) * mm, "end": v(-12.14, 6.5) * mm});
            skLineSegment(sketch, "E184.trimOffspring", {"start": v(0, 15.5) * mm, "end": v(12.14, 6.5) * mm});
            skLineSegment(sketch, "E185.trimOffspring", {"start": v(-3.36, 18) * mm, "end": v(-15.5, 9) * mm});
            skLineSegment(sketch, "E186.trimOffspring", {"start": v(3.36, 18) * mm, "end": v(15.5, 9) * mm});
            skSolve(sketch);
        }
        {
            var Q0;
            Q0 = qSketchRegion(id + "F32", true);
            extrude(context, id + "F33", {"entities" : qUnion([Q0]), "depth" : 1.5 * mm});
        }
        {
            var Q0;
            Q0=qCreatedBy(makeId("Top.planeOp"),FACE);
            var sketch = newSketch(context, id + "F34", { "sketchPlane" : qUnion([Q0])});
            skCircle(sketch, "E187", {"center": v(0, 0) * mm, "radius": 3 * mm});
            skCircle(sketch, "E188", {"center": v(0, 0) * mm, "radius": 1.5 * mm});
            skSolve(sketch);
        }
        {
            var Q0;
            Q0=makeQuery(id+"F34.imprint","IMPRINT",FACE,{"disambiguationData":[TD([[makeQuery(id+"F34.imprint","IMPRINT",EDGE,{"derivedFrom":sQuery(id+"F34.wireOp",EDGE,"E188")}),1.0]])]});
            extrude(context, id + "F35", {"entities" : qUnion([Q0]), "depth" : 12 * mm});
        }
        {
            var Q0;
            Q0 = qSketchRegion(id + "F34", true);
            extrude(context, id + "F36", {"entities" : qUnion([Q0]), "operationType" : NewBodyOperationType.ADD, "depth" : 2 * mm});
        }
    });
